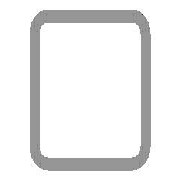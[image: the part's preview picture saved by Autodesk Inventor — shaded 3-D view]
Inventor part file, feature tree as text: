
AUTODESK INVENTOR PART (.ipt)
format: ipt  version: 2025 (Build 290162010, 162A)  size: 146,432 bytes
history: native  units: mm (DEFAULTED — no unit token found)
features: other x3, sketch x1, plane x1
ambient origin geometry x8: Origin, YZ Plane, XZ Plane, XY Plane, X Axis, Y Axis, Z Axis, Center Point
bodies: Solid1 (feature_tree), Body (feature_tree)
feature tree (5):
  other  "Driven Length"
  other  "Start plane"
  other  "End plane"
  sketch  "Sketch3"  dims[d3=8000.0mm d4=0.0mm d7=6.0mm d9=100.0mm d11=100.0mm d12=3.0mm d13=-0.0mm d14=8000.0mm d15=50.0mm d16=50.0mm d17=90.0deg d18=8000.0mm]
  plane  "Work Plane3"
